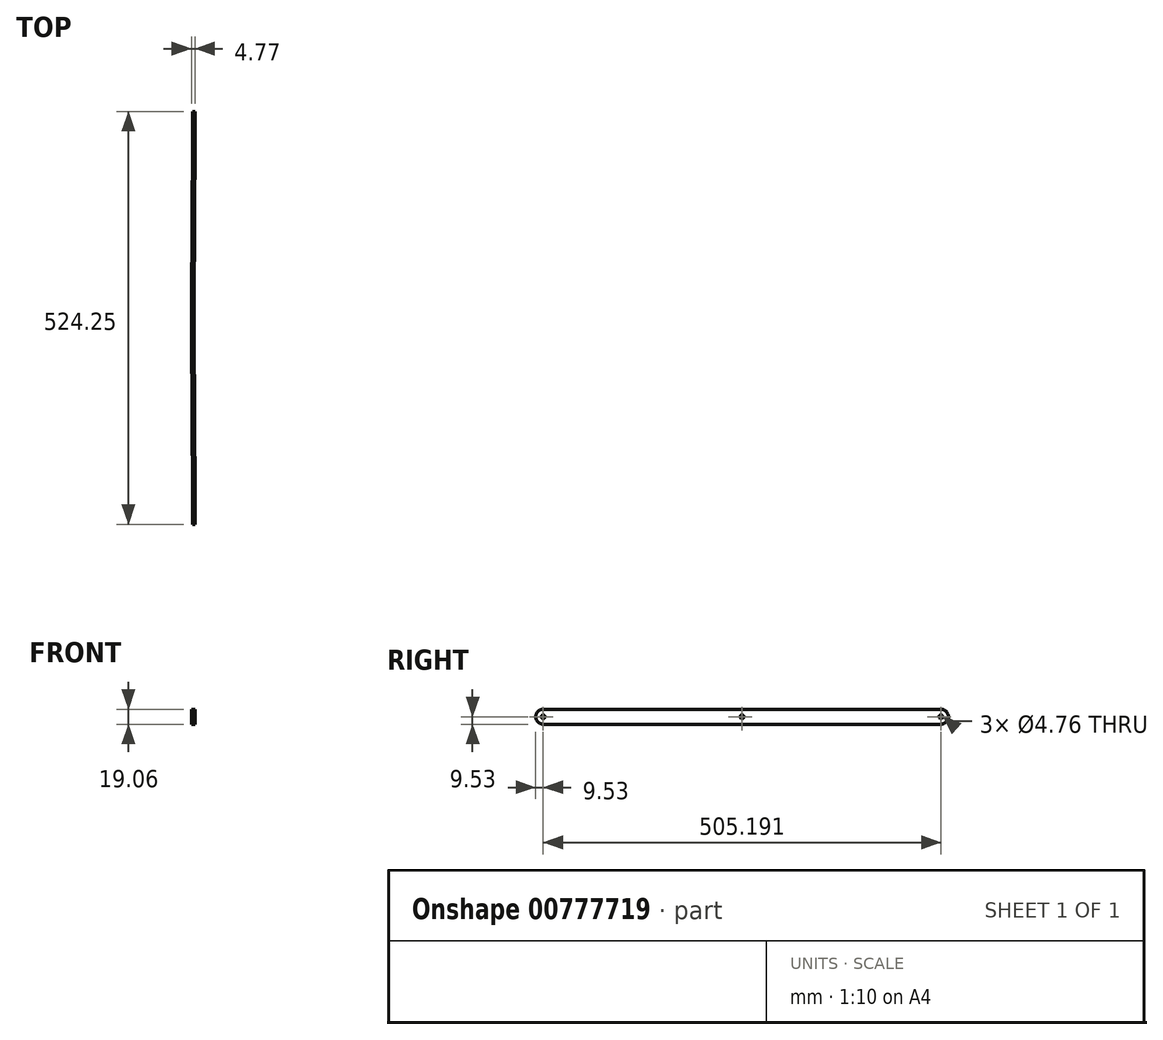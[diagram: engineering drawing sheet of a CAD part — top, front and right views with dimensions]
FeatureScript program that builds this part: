
annotation { "Feature Type Name" : "Feature", "Feature Type Description" : "" }
export const myFeature = defineFeature(function(context is Context, id is Id, definition is map)
    precondition{}
    {
        {
            var Q0;
            Q0=qCreatedBy(makeId("Right.planeOp"),FACE);
            var sketch = newSketch(context, id + "F0", { "sketchPlane" : qUnion([Q0])});
            skLineSegment(sketch, "E0.bottom", {"start": v(0, 9.53) * mm, "end": v(505.2, 9.53) * mm});
            skLineSegment(sketch, "E0.top", {"start": v(0, -9.53) * mm, "end": v(505.2, -9.53) * mm});
            skArc(sketch, "E1.filletArc", {"start": v(0, 9.52) * mm, "mid": v(-9.53, 0) * mm, "end": v(0, -9.53) * mm});
            skArc(sketch, "E2.filletArc", {"start": v(505.2, -9.53) * mm, "mid": v(514.72, 0) * mm, "end": v(505.2, 9.53) * mm});
            skCircle(sketch, "E3", {"center": v(0, 0) * mm, "radius": 2.38 * mm});
            skCircle(sketch, "E4", {"center": v(505.2, 0) * mm, "radius": 2.38 * mm});
            skCircle(sketch, "E5", {"center": v(252.6, 0) * mm, "radius": 2.38 * mm});
            skSolve(sketch);
        }
        {
            var Q0;
            Q0 = qSketchRegion(id + "F0", true);
            extrude(context, id + "F1", {"entities" : qUnion([Q0]), "depth" : 3.17 * mm, "offsetDistance" : 25.4 * mm});
        }
        {
            var Q0;
            Q0=makeQuery(id+"F1.opExtrude","SWEPT_FACE",FACE,{"disambiguationData":[OSD([sQuery(id+"F0.wireOp",EDGE,"E0.bottom")])]});
            var sketch = newSketch(context, id + "F2", { "sketchPlane" : qUnion([Q0])});
            skLineSegment(sketch, "E6", {"start": v(0, 25.4) * mm, "end": v(-1.59, 233.55) * mm});
            skLineSegment(sketch, "E7", {"start": v(-1.59, 233.55) * mm, "end": v(-1.59, 271.65) * mm});
            skLineSegment(sketch, "E8", {"start": v(-1.59, 271.65) * mm, "end": v(0, 479.8) * mm});
            skLineSegment(sketch, "E9", {"start": v(0, 25.4) * mm, "end": v(0, 479.8) * mm});
            skSolve(sketch);
        }
        {
            var Q0;
            Q0 = qSketchRegion(id + "F2", true);
            extrude(context, id + "F3", {"entities" : qUnion([Q0]), "operationType" : NewBodyOperationType.ADD, "oppositeDirection" : true, "depth" : 19.05 * mm, "offsetDistance" : 25.4 * mm});
        }
        {
            var Q0;
            Q0=makeQuery(id+"F3.boolean.opBoolean","MERGE",FACE,{"derivedFrom":[makeQuery(id+"F1.opExtrude","SWEPT_FACE",FACE,{"disambiguationData":[OSD([sQuery(id+"F0.wireOp",EDGE,"E0.bottom")])]}),makeQuery(id+"F3.opExtrude","CAP_FACE",FACE,{"disambiguationData":[OSD([sQuery(id+"F2.wireOp",EDGE,"E6"),sQuery(id+"F2.wireOp",EDGE,"E7"),sQuery(id+"F2.wireOp",EDGE,"E8"),sQuery(id+"F2.wireOp",EDGE,"E9")])],"isStart":true})]});
            var sketch = newSketch(context, id + "F4", { "sketchPlane" : qUnion([Q0])});
            skLineSegment(sketch, "E10.0.0", {"start": v(0, 25.4) * mm, "end": v(0, 0) * mm});
            skLineSegment(sketch, "E10.0.1", {"start": v(0, 0) * mm, "end": v(3.18, 0) * mm});
            skLineSegment(sketch, "E10.0.2", {"start": v(3.18, 0) * mm, "end": v(3.18, 505.2) * mm});
            skLineSegment(sketch, "E10.0.3", {"start": v(3.18, 505.2) * mm, "end": v(0, 505.2) * mm});
            skLineSegment(sketch, "E10.0.4", {"start": v(0, 505.2) * mm, "end": v(0, 479.8) * mm});
            skLineSegment(sketch, "E10.0.5", {"start": v(0, 479.8) * mm, "end": v(-1.59, 271.65) * mm});
            skLineSegment(sketch, "E10.0.6", {"start": v(-1.59, 271.65) * mm, "end": v(-1.59, 233.55) * mm});
            skLineSegment(sketch, "E10.0.7", {"start": v(-1.59, 233.55) * mm, "end": v(0, 25.4) * mm});
            skLineSegment(sketch, "E11.0", {"start": v(1.59, 233.56) * mm, "end": v(3.18, 25.41) * mm});
            skLineSegment(sketch, "E11.1", {"start": v(1.59, 271.63) * mm, "end": v(1.59, 233.56) * mm});
            skLineSegment(sketch, "E11.2", {"start": v(3.18, 479.78) * mm, "end": v(1.59, 271.63) * mm});
            skSolve(sketch);
        }
        {
            var Q0;
            {var subQ0=sQuery(id+"F4.wireOp",EDGE,"E11.0");Q0=makeQuery(id+"F4.imprint","IMPRINT",FACE,{"disambiguationData":[TD([[makeQuery(id+"F4.imprint","IMPRINT",EDGE,{"derivedFrom":subQ0}),1.0]])]});}
            extrude(context, id + "F5", {"entities" : qUnion([Q0]), "operationType" : NewBodyOperationType.REMOVE, "oppositeDirection" : true, "depth" : 25.4 * mm, "offsetDistance" : 25.4 * mm});
        }
        {
            var Q0;
            Q0=makeQuery(id+"F5.boolean.opBoolean","COPY",FACE,{"derivedFrom":makeQuery(id+"F5.opExtrude","SWEPT_FACE",FACE,{"disambiguationData":[OSD([sQuery(id+"F4.wireOp",EDGE,"E11.1")])]})});
            var sketch = newSketch(context, id + "F6", { "sketchPlane" : qUnion([Q0])});
            skCircle(sketch, "E12", {"center": v(252.6, 0) * mm, "radius": 2.38 * mm});
            skSolve(sketch);
        }
        {
            var Q0;
            Q0 = qSketchRegion(id + "F6", true);
            extrude(context, id + "F7", {"entities" : qUnion([Q0]), "operationType" : NewBodyOperationType.REMOVE, "oppositeDirection" : true, "depth" : 25.4 * mm, "offsetDistance" : 25.4 * mm});
        }
    });
